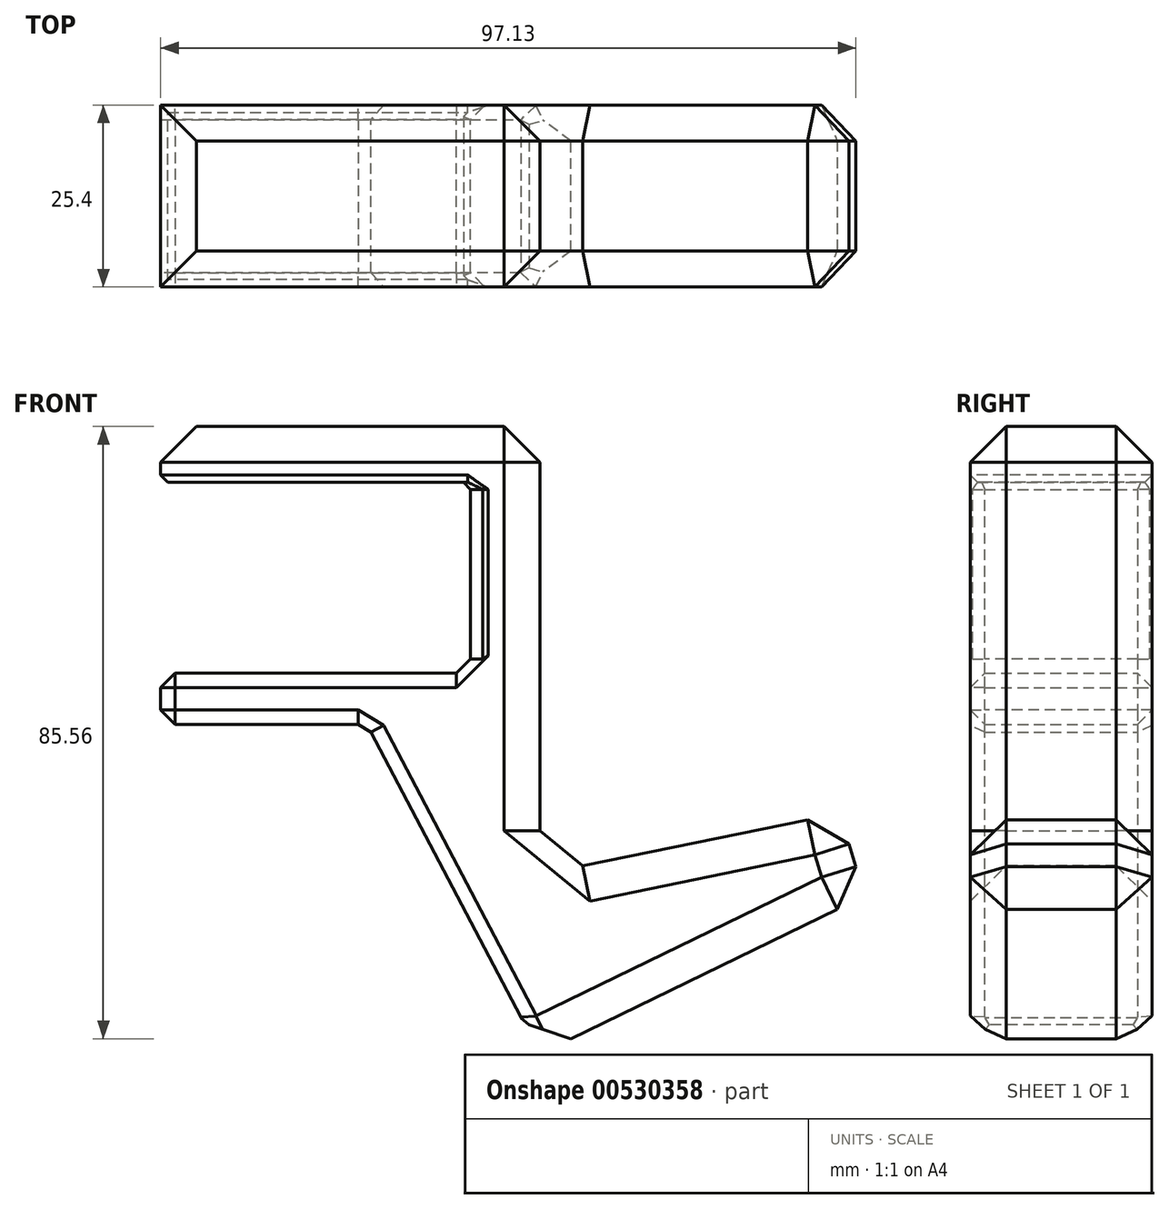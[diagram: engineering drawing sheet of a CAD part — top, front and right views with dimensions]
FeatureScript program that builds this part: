
annotation { "Feature Type Name" : "Feature", "Feature Type Description" : "" }
export const myFeature = defineFeature(function(context is Context, id is Id, definition is map)
    precondition{}
    {
        {
            var Q0;
            Q0=qCreatedBy(makeId("Front.planeOp"),FACE);
            var sketch = newSketch(context, id + "F0", { "sketchPlane" : qUnion([Q0])});
            skLineSegment(sketch, "E0", {"start": v(0, -43.63) * mm, "end": v(45.41, -21.55) * mm});
            skLineSegment(sketch, "E1", {"start": v(45.41, -21.55) * mm, "end": v(41.84, -9.99) * mm});
            skLineSegment(sketch, "E2", {"start": v(41.84, -9.99) * mm, "end": v(0, -18.6) * mm});
            skLineSegment(sketch, "E3", {"start": v(0, -18.6) * mm, "end": v(0, 44.05) * mm});
            skLineSegment(sketch, "E4", {"start": v(0, 44.05) * mm, "end": v(-52.98, 44.05) * mm});
            skLineSegment(sketch, "E5", {"start": v(-52.98, 44.05) * mm, "end": v(-52.98, 36.27) * mm});
            skLineSegment(sketch, "E6", {"start": v(-52.98, 36.27) * mm, "end": v(-9.67, 36.27) * mm});
            skLineSegment(sketch, "E7", {"start": v(-9.67, 36.27) * mm, "end": v(-9.67, 9.57) * mm});
            skLineSegment(sketch, "E8", {"start": v(-9.67, 9.57) * mm, "end": v(-52.98, 9.57) * mm});
            skLineSegment(sketch, "E9", {"start": v(-52.98, 9.57) * mm, "end": v(-52.98, 2.42) * mm});
            skLineSegment(sketch, "E10", {"start": v(-52.98, 2.42) * mm, "end": v(-24.18, 2.42) * mm});
            skLineSegment(sketch, "E11", {"start": v(-24.18, 2.42) * mm, "end": v(0, -43.63) * mm});
            skSolve(sketch);
        }
        {
            var Q0;
            Q0 = qSketchRegion(id + "F0", true);
            extrude(context, id + "F1", {"entities" : qUnion([Q0]), "endBound" : BoundingType.SYMMETRIC, "depth" : 25.4 * mm, "offsetDistance" : 25.4 * mm});
        }
        {
            var Q0;
            Q0=makeQuery(id+"F1.opExtrude","SWEPT_FACE",FACE,{"disambiguationData":[OSD([sQuery(id+"F0.wireOp",EDGE,"E1")])]});
            var Q1;
            Q1=makeQuery(id+"F1.opExtrude","SWEPT_FACE",FACE,{"disambiguationData":[OSD([sQuery(id+"F0.wireOp",EDGE,"E2")])]});
            var Q2;
            Q2=makeQuery(id+"F1.opExtrude","SWEPT_FACE",FACE,{"disambiguationData":[OSD([sQuery(id+"F0.wireOp",EDGE,"E4")])]});
            var Q3;
            Q3=makeQuery(id+"F1.opExtrude","SWEPT_FACE",FACE,{"disambiguationData":[OSD([sQuery(id+"F0.wireOp",EDGE,"E0")])]});
            chamfer(context, id + "F2", {"entities" : qUnion([Q0, Q1, Q2, Q3]), "width" : 5 * mm, "tangentPropagation" : true});
        }
        {
            var Q0;
            Q0=makeQuery(id+"F1.opExtrude","SWEPT_FACE",FACE,{"disambiguationData":[OSD([sQuery(id+"F0.wireOp",EDGE,"E11")])]});
            var Q1;
            Q1=makeQuery(id+"F1.opExtrude","SWEPT_FACE",FACE,{"disambiguationData":[OSD([sQuery(id+"F0.wireOp",EDGE,"E9")])]});
            var Q2;
            Q2=makeQuery(id+"F1.opExtrude","SWEPT_FACE",FACE,{"disambiguationData":[OSD([sQuery(id+"F0.wireOp",EDGE,"E8")])]});
            chamfer(context, id + "F3", {"entities" : qUnion([Q0, Q1, Q2]), "width" : 2 * mm, "tangentPropagation" : true});
        }
        {
            var Q0;
            Q0=makeQuery(id+"F1.opExtrude","SWEPT_FACE",FACE,{"disambiguationData":[OSD([sQuery(id+"F0.wireOp",EDGE,"E6")])]});
            chamfer(context, id + "F4", {"entities" : qUnion([Q0]), "width" : 1 * mm, "tangentPropagation" : true});
        }
    });
